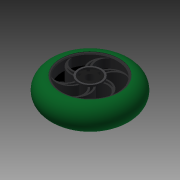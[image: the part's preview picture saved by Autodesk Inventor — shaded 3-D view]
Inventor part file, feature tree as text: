
AUTODESK INVENTOR PART (.ipt)
format: ipt  version: 2015 (Build 190159000, 159)  size: 855,552 bytes
history: native  units: in
note: dims shown in document units (in); Inventor stores cm internally (conversion verified against a paired STEP export)
features: sketch x14, extrude x11, mirror x6, sweep x1, chamfer x1, projected_geometry x1
ambient origin geometry x8: Origin, YZ Plane, XZ Plane, XY Plane, X Axis, Y Axis, Z Axis, Center Point
bodies: Solid1 (feature_tree)
feature tree (34):
  sweep  "Sweep1"
  sketch  "Sketch3"  dims[d18=0.0625in d19=0.0in d20=0.25in d21=0.0in]
  sketch  "Sketch6"  dims[d22=0.0625in d23=0.0in d24=0.0625in d25=0.0in]
  extrude  "Extrusion4"  Depth=1.75in
  extrude  "Extrusion5"  Depth=0.0625in TaperAngle=0.0deg
  extrude  "Extrusion6"  Depth=0.0625in TaperAngle=0.0deg
  mirror  "Mirror1"
  extrude  "Extrusion7"  Depth=0.24in TaperAngle=0.0deg
  mirror  "Mirror2"
  sketch  "Sketch11"  dims[d38=0.025in d39=0.125in d40=45.0deg d105=0.25in]
  extrude  "Extrusion8"  Depth=0.0625in TaperAngle=0.0deg
  extrude  "Extrusion9"  Depth=0.65in TaperAngle=0.0deg
  mirror  "Mirror3"
  extrude  "Extrusion10"  Depth=0.125in
  mirror  "Mirror4"
  extrude  "Extrusion11"  [1 undecoded]
  mirror  "Mirror5"
  extrude  "Extrusion12"  [1 undecoded]
  mirror  "Mirror6"
  extrude  "Extrusion13"  [1 undecoded]
  chamfer  "Chamfer1"  [1 undecoded]
  extrude  "Extrusion26"  [1 undecoded]
  sketch  "Sketch1"  dims[d0=2.5in d1=0.75in]
  sketch  "Sketch2"  dims[d2=0.0in d3=0.0in d4=1.75in]
  sketch  "Sketch7"  dims[d26=0.25in d27=0.0in d28=0.24in d29=0.0in]
  sketch  "Sketch9"  dims[d30=0.2in d31=0.0in d32=0.0625in d33=0.0in]
  sketch  "Sketch10"  dims[d34=0.05in d35=0.0in d36=0.65in d37=0.0in]
  sketch  "Sketch12"  dims[d106=1.0in d107=0.0in]
  sketch  "Sketch14"
  projected_geometry  "Projected Loop2"
  sketch  "Sketch15"
  sketch  "Sketch16"
  sketch  "Sketch18"
  sketch  "Sketch35"
note: 5 required parameter values undecoded (feature->parameter linkage not recoverable at this tier; creation-order binding heuristic only, values carry confidence <= 0.55)
